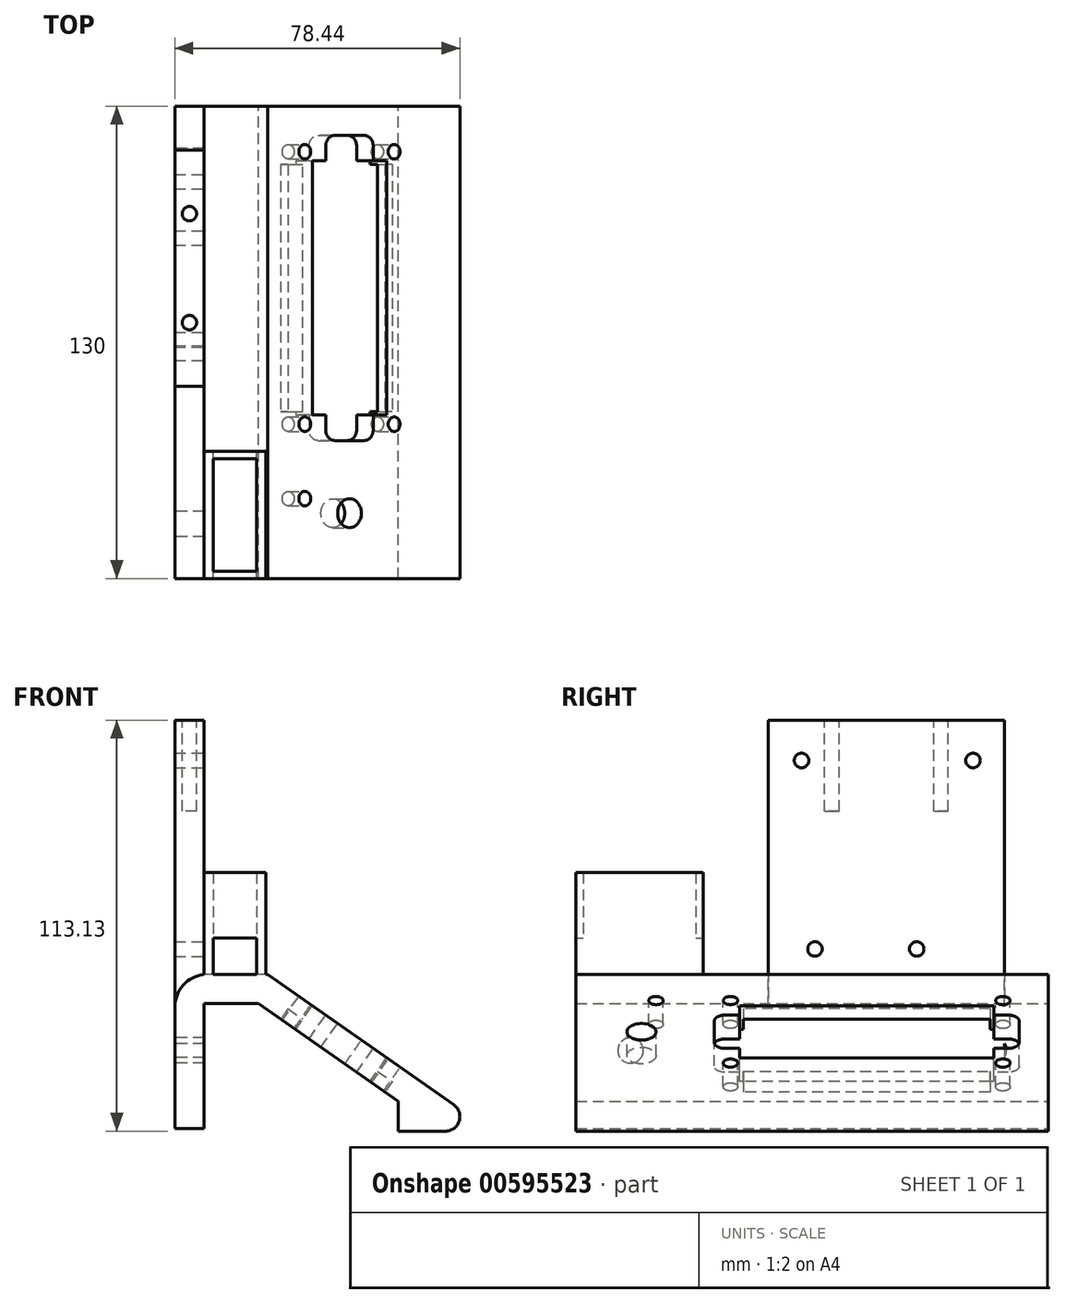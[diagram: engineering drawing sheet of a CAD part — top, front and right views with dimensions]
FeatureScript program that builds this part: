
annotation { "Feature Type Name" : "Feature", "Feature Type Description" : "" }
export const myFeature = defineFeature(function(context is Context, id is Id, definition is map)
    precondition{}
    {
        {
            var Q0;
            Q0=qCreatedBy(makeId("Front.planeOp"),FACE);
            var sketch = newSketch(context, id + "F0", { "sketchPlane" : qUnion([Q0])});
            skLineSegment(sketch, "E0", {"start": v(45.94, 7.5) * mm, "end": v(7.5, 34.41) * mm});
            skLineSegment(sketch, "E1", {"start": v(7.5, 34.41) * mm, "end": v(-7.5, 34.41) * mm});
            skLineSegment(sketch, "E2", {"start": v(-37.03, 0) * mm, "end": v(56.65, 0) * mm, "construction": true});
            skLineSegment(sketch, "E3", {"start": v(0, 34.41) * mm, "end": v(0, 0) * mm, "construction": true});
            skLineSegment(sketch, "E4.0", {"start": v(10.02, 42.41) * mm, "end": v(-7.5, 42.41) * mm});
            skLineSegment(sketch, "E4.1", {"start": v(61.24, 6.55) * mm, "end": v(10.02, 42.41) * mm});
            skLineSegment(sketch, "E5", {"start": v(-7.5, 42.41) * mm, "end": v(-7.5, 34.41) * mm, "construction": true});
            skLineSegment(sketch, "E6", {"start": v(61.24, 6.55) * mm, "end": v(56.65, 0) * mm, "construction": true});
            skArc(sketch, "E7", {"start": v(56.65, 0) * mm, "mid": v(62.22, 0.98) * mm, "end": v(61.24, 6.55) * mm});
            skLineSegment(sketch, "E8", {"start": v(-7.5, 34.41) * mm, "end": v(-7.5, 0) * mm});
            skLineSegment(sketch, "E9.0", {"start": v(-15.5, 33.47) * mm, "end": v(-15.5, 0) * mm});
            skArc(sketch, "E10", {"start": v(-7.5, 42.41) * mm, "mid": v(-13.2, 39.47) * mm, "end": v(-15.5, 33.47) * mm});
            skLineSegment(sketch, "E11", {"start": v(-7.5, 0) * mm, "end": v(-15.5, 0) * mm});
            skLineSegment(sketch, "E12.bottom", {"start": v(58.94, -0.72) * mm, "end": v(45.94, -0.72) * mm});
            skLineSegment(sketch, "E13", {"start": v(45.94, -0.72) * mm, "end": v(45.94, 7.5) * mm});
            skSolve(sketch);
        }
        {
            var Q0;
            Q0=makeQuery(id+"F0.imprint","IMPRINT",FACE,{"disambiguationData":[TD([[makeQuery(id+"F0.imprint","IMPRINT",EDGE,{"derivedFrom":sQuery(id+"F0.wireOp",EDGE,"E0")}),-1.0]])]});
            extrude(context, id + "F1", {"entities" : qUnion([Q0]), "depth" : 80 * mm, "offsetDistance" : 25 * mm, "hasSecondDirection" : true, "secondDirectionOppositeDirection" : true, "secondDirectionDepth" : 50 * mm});
        }
        {
            var Q0;
            Q0=makeQuery(id+"F1.opExtrude","SWEPT_FACE",FACE,{"disambiguationData":[OSD([sQuery(id+"F0.wireOp",EDGE,"E4.1")])]});
            var sketch = newSketch(context, id + "F2", { "sketchPlane" : qUnion([Q0])});
            skLineSegment(sketch, "E14.bottom", {"start": v(-1.1, -35) * mm, "end": v(3.4, -35) * mm});
            skLineSegment(sketch, "E14.top", {"start": v(-1.1, 35) * mm, "end": v(23.9, 35) * mm});
            skLineSegment(sketch, "E14.left", {"start": v(-1.1, -35) * mm, "end": v(-1.1, 35) * mm});
            skLineSegment(sketch, "E14.right", {"start": v(23.9, -35) * mm, "end": v(23.9, 35) * mm});
            skPoint(sketch, "E14.middle", {"position": v(11.4, 0) * mm});
            skLineSegment(sketch, "E15.bottom", {"start": v(26.4, 37.5) * mm, "end": v(-3.6, 37.5) * mm, "construction": true});
            skLineSegment(sketch, "E15.top", {"start": v(26.4, -37.5) * mm, "end": v(-3.6, -37.5) * mm, "construction": true});
            skLineSegment(sketch, "E15.left", {"start": v(26.4, 37.5) * mm, "end": v(26.4, -37.5) * mm, "construction": true});
            skLineSegment(sketch, "E15.right", {"start": v(-3.6, 37.5) * mm, "end": v(-3.6, -37.5) * mm, "construction": true});
            skCircle(sketch, "E16", {"center": v(-3.6, -37.5) * mm, "radius": 2 * mm});
            skCircle(sketch, "E17", {"center": v(-3.6, 37.5) * mm, "radius": 2 * mm});
            skCircle(sketch, "E18", {"center": v(26.4, 37.5) * mm, "radius": 2 * mm});
            skCircle(sketch, "E19", {"center": v(26.4, -37.5) * mm, "radius": 2 * mm});
            skLineSegment(sketch, "E20.bottom", {"start": v(6.4, -42) * mm, "end": v(16.4, -42) * mm});
            skLineSegment(sketch, "E20.top", {"start": v(3.4, -28) * mm, "end": v(19.4, -28) * mm, "construction": true});
            skLineSegment(sketch, "E20.left", {"start": v(3.4, -39) * mm, "end": v(3.4, -35) * mm});
            skLineSegment(sketch, "E20.right", {"start": v(19.4, -39) * mm, "end": v(19.4, -35) * mm});
            skPoint(sketch, "E20.middle", {"position": v(11.4, -35) * mm});
            skLineSegment(sketch, "E21", {"start": v(3.4, -35) * mm, "end": v(3.4, -28) * mm, "construction": true});
            skLineSegment(sketch, "E22", {"start": v(19.4, -35) * mm, "end": v(19.4, -28) * mm, "construction": true});
            skLineSegment(sketch, "E23", {"start": v(19.4, -35) * mm, "end": v(23.9, -35) * mm});
            skLineSegment(sketch, "E24", {"start": v(3.4, -35) * mm, "end": v(19.4, -35) * mm, "construction": true});
            skLineSegment(sketch, "E25", {"start": v(-16.12, -15) * mm, "end": v(46.4, -15) * mm, "construction": true});
            skPoint(sketch, "E26.visualSharp", {"position": v(3.4, -42) * mm});
            skArc(sketch, "E26.filletArc", {"start": v(3.4, -39) * mm, "mid": v(4.28, -41.12) * mm, "end": v(6.4, -42) * mm});
            skPoint(sketch, "E27.visualSharp", {"position": v(19.4, -42) * mm});
            skArc(sketch, "E27.filletArc", {"start": v(16.4, -42) * mm, "mid": v(18.53, -41.12) * mm, "end": v(19.4, -39) * mm});
            skLineSegment(sketch, "E28.bottom", {"start": v(3.4, 28) * mm, "end": v(19.4, 28) * mm, "construction": true});
            skLineSegment(sketch, "E28.top", {"start": v(6.4, 42) * mm, "end": v(16.4, 42) * mm});
            skLineSegment(sketch, "E28.left", {"start": v(3.4, 28) * mm, "end": v(3.4, 35) * mm, "construction": true});
            skLineSegment(sketch, "E28.right", {"start": v(19.4, 28) * mm, "end": v(19.4, 35) * mm, "construction": true});
            skPoint(sketch, "E28.middle", {"position": v(11.4, 35) * mm});
            skLineSegment(sketch, "E29", {"start": v(3.4, 35) * mm, "end": v(3.4, 35.04) * mm});
            skLineSegment(sketch, "E30", {"start": v(19.4, 35) * mm, "end": v(19.4, 35) * mm});
            skLineSegment(sketch, "E31", {"start": v(3.4, 35.04) * mm, "end": v(3.4, 39) * mm});
            skLineSegment(sketch, "E32", {"start": v(19.4, 35) * mm, "end": v(19.4, 39) * mm});
            skPoint(sketch, "E33.visualSharp", {"position": v(3.4, 42) * mm});
            skArc(sketch, "E33.filletArc", {"start": v(6.4, 42) * mm, "mid": v(4.28, 41.12) * mm, "end": v(3.4, 39) * mm});
            skPoint(sketch, "E34.visualSharp", {"position": v(19.4, 42) * mm});
            skArc(sketch, "E34.filletArc", {"start": v(19.4, 39) * mm, "mid": v(18.53, 41.12) * mm, "end": v(16.4, 42) * mm});
            skSolve(sketch);
        }
        {
            var Q0;
            Q0=qSketchRegion(id+"F2",true);
            extrude(context, id + "F3", {"entities" : qUnion([Q0]), "operationType" : NewBodyOperationType.REMOVE, "oppositeDirection" : true, "depth" : 25 * mm, "offsetDistance" : 25 * mm});
        }
        {
            var Q0;
            Q0=makeQuery(id+"F1.opExtrude","SWEPT_FACE",FACE,{"disambiguationData":[OSD([sQuery(id+"F0.wireOp",EDGE,"E4.0")])]});
            var sketch = newSketch(context, id + "F4", { "sketchPlane" : qUnion([Q0])});
            skLineSegment(sketch, "E35.bottom", {"start": v(9.5, -80) * mm, "end": v(9.5, -45) * mm});
            skLineSegment(sketch, "E35.top", {"start": v(-7.5, -80) * mm, "end": v(-7.5, -45) * mm});
            skLineSegment(sketch, "E35.left", {"start": v(9.5, -80) * mm, "end": v(-7.5, -80) * mm});
            skLineSegment(sketch, "E35.right", {"start": v(9.5, -45) * mm, "end": v(-7.5, -45) * mm});
            skLineSegment(sketch, "E36.bottom", {"start": v(7, -78) * mm, "end": v(7, -47) * mm});
            skLineSegment(sketch, "E36.top", {"start": v(-5, -78) * mm, "end": v(-5, -47) * mm});
            skLineSegment(sketch, "E36.left", {"start": v(7, -78) * mm, "end": v(-5, -78) * mm});
            skLineSegment(sketch, "E36.right", {"start": v(7, -47) * mm, "end": v(-5, -47) * mm});
            skLineSegment(sketch, "E37", {"start": v(1, -80) * mm, "end": v(1, -45) * mm, "construction": true});
            skLineSegment(sketch, "E38", {"start": v(9.5, -62.5) * mm, "end": v(-7.5, -62.5) * mm, "construction": true});
            skLineSegment(sketch, "E39", {"start": v(1, -78) * mm, "end": v(1, -47) * mm, "construction": true});
            skSolve(sketch);
        }
        {
            var Q0;
            Q0=qSketchRegion(id+"F4",true);
            extrude(context, id + "F5", {"entities" : qUnion([Q0]), "operationType" : NewBodyOperationType.ADD, "depth" : 28 * mm, "offsetDistance" : 25 * mm});
        }
        {
            var Q0;
            Q0=makeQuery(id+"F5.opExtrude","SWEPT_FACE",FACE,{"disambiguationData":[OSD([sQuery(id+"F4.wireOp",EDGE,"E35.right")])]});
            var sketch = newSketch(context, id + "F6", { "sketchPlane" : qUnion([Q0])});
            skLineSegment(sketch, "E40.bottom", {"start": v(-7, 42.41) * mm, "end": v(5, 42.41) * mm});
            skLineSegment(sketch, "E40.top", {"start": v(-7, 52.41) * mm, "end": v(5, 52.41) * mm});
            skLineSegment(sketch, "E40.left", {"start": v(-7, 42.41) * mm, "end": v(-7, 52.41) * mm});
            skLineSegment(sketch, "E40.right", {"start": v(5, 42.41) * mm, "end": v(5, 52.41) * mm});
            skPoint(sketch, "E40.middle", {"position": v(-1, 47.41) * mm});
            skLineSegment(sketch, "E41.bottom", {"start": v(-1, 42.41) * mm, "end": v(-1, 42.41) * mm});
            skLineSegment(sketch, "E41.top", {"start": v(-1, 98.41) * mm, "end": v(-1, 98.41) * mm});
            skLineSegment(sketch, "E41.left", {"start": v(-1, 42.41) * mm, "end": v(-1, 98.41) * mm});
            skLineSegment(sketch, "E41.right", {"start": v(-1, 42.41) * mm, "end": v(-1, 98.41) * mm, "construction": true});
            skPoint(sketch, "E41.middle", {"position": v(-1, 70.41) * mm});
            skSolve(sketch);
        }
        {
            var Q0;
            Q0=qSketchRegion(id+"F6",true);
            extrude(context, id + "F7", {"entities" : qUnion([Q0]), "operationType" : NewBodyOperationType.REMOVE, "endBound" : BoundingType.THROUGH_ALL, "oppositeDirection" : true, "depth" : 25 * mm, "offsetDistance" : 25 * mm});
        }
        {
            var Q0;
            Q0=makeQuery(id+"F1.opExtrude","SWEPT_FACE",FACE,{"disambiguationData":[OSD([sQuery(id+"F0.wireOp",EDGE,"E4.1")])]});
            var sketch = newSketch(context, id + "F8", { "sketchPlane" : qUnion([Q0])});
            skCircle(sketch, "E42", {"center": v(11.4, -62) * mm, "radius": 4 * mm});
            skCircle(sketch, "E43", {"center": v(-3.6, -58) * mm, "radius": 2 * mm});
            skSolve(sketch);
        }
        {
            var Q0;
            Q0=qSketchRegion(id+"F8",true);
            extrude(context, id + "F9", {"entities" : qUnion([Q0]), "operationType" : NewBodyOperationType.REMOVE, "oppositeDirection" : true, "depth" : 25 * mm, "offsetDistance" : 25 * mm});
        }
        {
            var Q0;
            Q0=makeQuery(id+"F1.opExtrude","SWEPT_FACE",FACE,{"disambiguationData":[OSD([sQuery(id+"F0.wireOp",EDGE,"E9.0")])]});
            var sketch = newSketch(context, id + "F10", { "sketchPlane" : qUnion([Q0])});
            skCircle(sketch, "E44", {"center": v(-35, 21.47) * mm, "radius": 3.5 * mm});
            skLineSegment(sketch, "E45", {"start": v(15, 33.47) * mm, "end": v(15, 0) * mm, "construction": true});
            skCircle(sketch, "E46.MirrorC", {"center": v(65, 21.47) * mm, "radius": 3.5 * mm});
            skSolve(sketch);
        }
        {
            var Q0;
            Q0=qSketchRegion(id+"F10",true);
            extrude(context, id + "F11", {"entities" : qUnion([Q0]), "operationType" : NewBodyOperationType.REMOVE, "endBound" : BoundingType.UP_TO_NEXT, "oppositeDirection" : true, "depth" : 25 * mm, "offsetDistance" : 25 * mm});
        }
        {
            var Q0;
            {var subQ0=sQuery(id+"F0.wireOp",EDGE,"E4.0");var subQ1=makeQuery(id+"F1.opExtrude","SWEPT_FACE",FACE,{"disambiguationData":[OSD([subQ0])]});var subQ7=sQuery(id+"F0.wireOp",EDGE,"E4.1");Q0=makeQuery(id+"F7.boolean.opBoolean","MERGE",FACE,{"derivedFrom":[makeQuery(id+"F5.boolean.opBoolean","SPLIT",FACE,{"disambiguationData":[TD([makeQuery(id+"F1.opExtrude","SWEPT_FACE",FACE,{"disambiguationData":[OSD([subQ7])]})])],"derivedFrom":subQ1}),makeQuery(id+"F5.boolean.opBoolean","SPLIT",FACE,{"disambiguationData":[TD([makeQuery(id+"F5.opExtrude","SWEPT_FACE",FACE,{"disambiguationData":[OSD([sQuery(id+"F4.wireOp",EDGE,"E36.bottom")])]})])],"derivedFrom":subQ1}),makeQuery(id+"F7.opExtrude","SWEPT_FACE",FACE,{"disambiguationData":[OSD([sQuery(id+"F6.wireOp",EDGE,"E40.bottom")])]})]});}
            var sketch = newSketch(context, id + "F12", { "sketchPlane" : qUnion([Q0])});
            skLineSegment(sketch, "E47.bottom", {"start": v(-15.5, 37.95) * mm, "end": v(-7.5, 37.95) * mm});
            skLineSegment(sketch, "E47.top", {"start": v(-15.5, -27.05) * mm, "end": v(-7.5, -27.05) * mm});
            skLineSegment(sketch, "E47.left", {"start": v(-15.5, 37.95) * mm, "end": v(-15.5, -27.05) * mm});
            skLineSegment(sketch, "E47.right", {"start": v(-7.5, 37.95) * mm, "end": v(-7.5, -27.05) * mm});
            skSolve(sketch);
        }
        {
            var Q0;
            Q0=qSketchRegion(id+"F12",true);
            extrude(context, id + "F13", {"entities" : qUnion([Q0]), "operationType" : NewBodyOperationType.ADD, "depth" : 70 * mm, "offsetDistance" : 25 * mm, "hasSecondDirection" : true, "secondDirectionOppositeDirection" : true, "secondDirectionDepth" : 25 * mm});
        }
        {
            var Q0;
            Q0=makeQuery(id+"F13.opExtrude","CAP_FACE",FACE,{"disambiguationData":[OSD([sQuery(id+"F12.wireOp",EDGE,"E47.bottom"),sQuery(id+"F12.wireOp",EDGE,"E47.top"),sQuery(id+"F12.wireOp",EDGE,"E47.left"),sQuery(id+"F12.wireOp",EDGE,"E47.right")])],"isStart":false});
            var sketch = newSketch(context, id + "F14", { "sketchPlane" : qUnion([Q0])});
            skCircle(sketch, "E48", {"center": v(-11.5, -9.55) * mm, "radius": 2 * mm});
            skLineSegment(sketch, "E49", {"start": v(-11.5, -27.05) * mm, "end": v(-11.5, 37.95) * mm, "construction": true});
            skLineSegment(sketch, "E50", {"start": v(-15.5, 5.45) * mm, "end": v(-7.5, 5.45) * mm, "construction": true});
            skCircle(sketch, "E51.MirrorC", {"center": v(-11.5, 20.45) * mm, "radius": 2 * mm});
            skSolve(sketch);
        }
        {
            var Q0;
            Q0=qSketchRegion(id+"F14",true);
            extrude(context, id + "F15", {"entities" : qUnion([Q0]), "operationType" : NewBodyOperationType.REMOVE, "oppositeDirection" : true, "depth" : 25 * mm, "offsetDistance" : 25 * mm});
        }
        {
            var Q0;
            Q0=makeQuery(id+"F13.opExtrude","SWEPT_FACE",FACE,{"disambiguationData":[OSD([sQuery(id+"F12.wireOp",EDGE,"E47.right")])]});
            var sketch = newSketch(context, id + "F16", { "sketchPlane" : qUnion([Q0])});
            skLineSegment(sketch, "E52.bottom", {"start": v(32.77, 115.41) * mm, "end": v(-21.23, 115.41) * mm, "construction": true});
            skLineSegment(sketch, "E52.top", {"start": v(32.77, 45.41) * mm, "end": v(-21.23, 45.41) * mm, "construction": true});
            skLineSegment(sketch, "E52.left", {"start": v(32.77, 115.41) * mm, "end": v(32.77, 45.41) * mm, "construction": true});
            skLineSegment(sketch, "E52.right", {"start": v(-21.23, 115.41) * mm, "end": v(-21.23, 45.41) * mm, "construction": true});
            skPoint(sketch, "E52.middle", {"position": v(5.77, 80.41) * mm});
            skLineSegment(sketch, "E53", {"start": v(45.77, 80.2) * mm, "end": v(-36.76, 80.2) * mm, "construction": true});
            skLineSegment(sketch, "E54", {"start": v(5.77, 130.2) * mm, "end": v(5.77, 103.92) * mm, "construction": true});
            skPoint(sketch, "E54.startSnap0", {"position": v(4.5, 130.2) * mm});
            skCircle(sketch, "E55", {"center": v(13.77, 49.41) * mm, "radius": 2 * mm});
            skCircle(sketch, "E56", {"center": v(-14.23, 49.41) * mm, "radius": 2 * mm});
            skCircle(sketch, "E57", {"center": v(29.27, 101.31) * mm, "radius": 2 * mm});
            skCircle(sketch, "E58", {"center": v(-17.93, 101.31) * mm, "radius": 2 * mm});
            skSolve(sketch);
        }
        {
            var Q0;
            Q0 = qSketchRegion(id + "F16", true);
            extrude(context, id + "F17", {"entities" : qUnion([Q0]), "operationType" : NewBodyOperationType.REMOVE, "oppositeDirection" : true, "depth" : 25 * mm, "offsetDistance" : 25 * mm});
        }
        {
            var Q0;
            Q0=makeQuery(id+"F1.opExtrude","SWEPT_FACE",FACE,{"disambiguationData":[OSD([sQuery(id+"F0.wireOp",EDGE,"E0")])]});
            var sketch = newSketch(context, id + "F18", { "sketchPlane" : qUnion([Q0])});
            skLineSegment(sketch, "E59.bottom", {"start": v(-6.1, -34) * mm, "end": v(28.9, -34) * mm});
            skLineSegment(sketch, "E59.top", {"start": v(-6.1, 34) * mm, "end": v(28.9, 34) * mm});
            skLineSegment(sketch, "E59.left", {"start": v(-6.1, -34) * mm, "end": v(-6.1, 34) * mm});
            skLineSegment(sketch, "E59.right", {"start": v(28.9, -34) * mm, "end": v(28.9, 34) * mm});
            skSolve(sketch);
        }
        {
            var Q0;
            Q0 = qSketchRegion(id + "F18", true);
            extrude(context, id + "F19", {"entities" : qUnion([Q0]), "operationType" : NewBodyOperationType.REMOVE, "oppositeDirection" : true, "depth" : 3.5 * mm, "offsetDistance" : 25 * mm});
        }
    });
